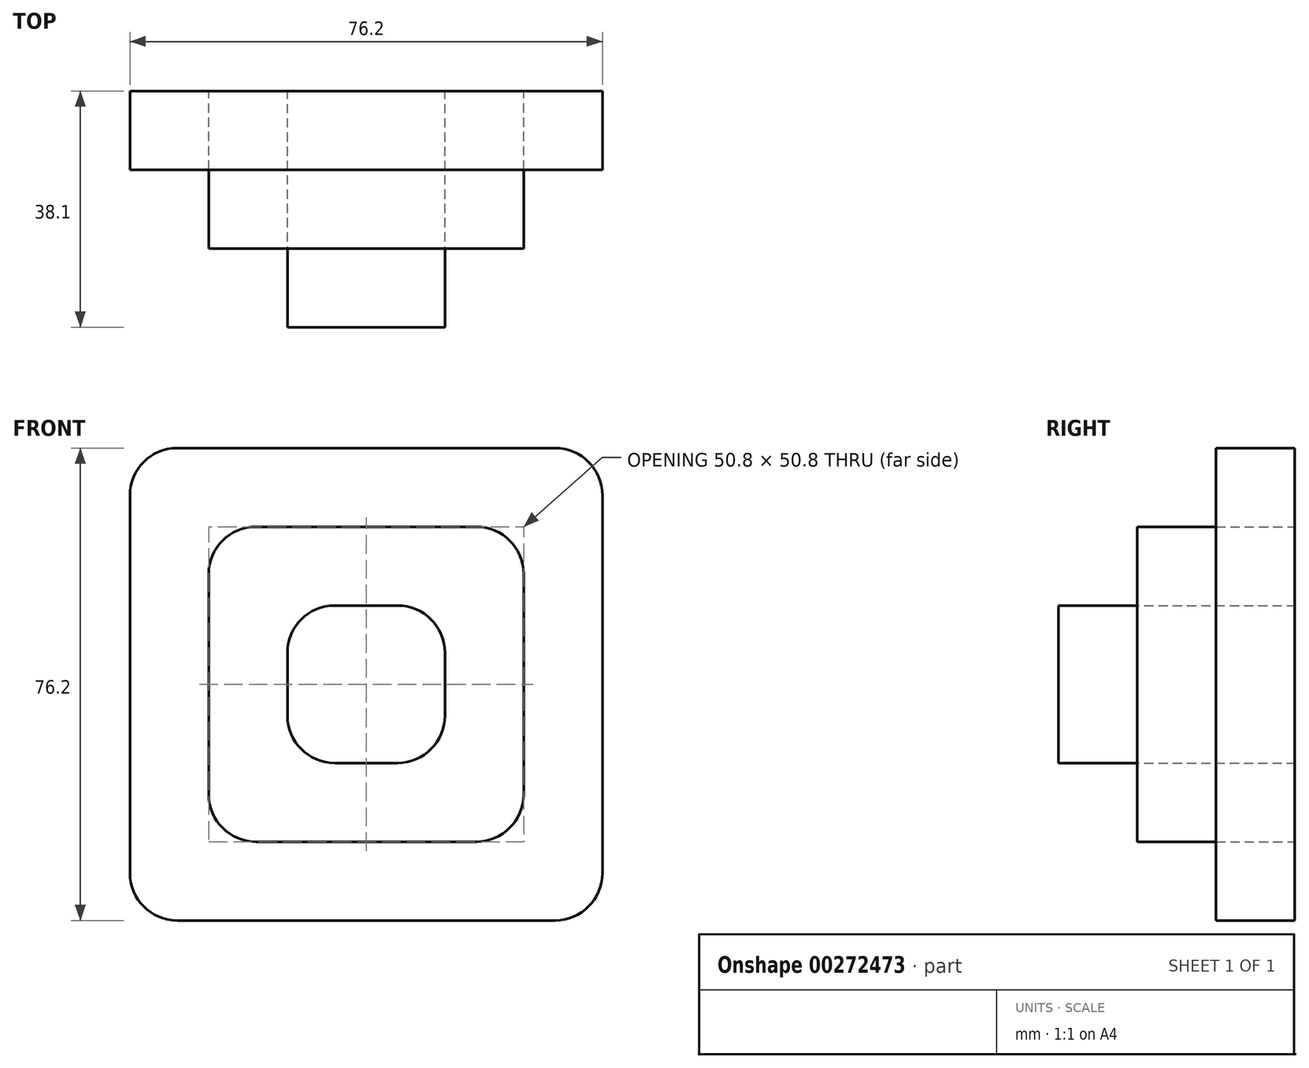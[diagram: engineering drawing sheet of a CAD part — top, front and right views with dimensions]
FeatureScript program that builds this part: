
annotation { "Feature Type Name" : "Feature", "Feature Type Description" : "" }
export const myFeature = defineFeature(function(context is Context, id is Id, definition is map)
    precondition{}
    {
        {
            var Q0;
            Q0=qCreatedBy(makeId("Front.planeOp"),FACE);
            var sketch = newSketch(context, id + "F0", { "sketchPlane" : qUnion([Q0])});
            skLineSegment(sketch, "E0.bottom", {"start": v(30.48, -38.1) * mm, "end": v(-30.48, -38.1) * mm});
            skLineSegment(sketch, "E0.top", {"start": v(30.48, 38.1) * mm, "end": v(-30.48, 38.1) * mm});
            skLineSegment(sketch, "E0.left", {"start": v(38.1, -30.48) * mm, "end": v(38.1, 30.48) * mm});
            skLineSegment(sketch, "E0.right", {"start": v(-38.1, -30.48) * mm, "end": v(-38.1, 30.48) * mm});
            skPoint(sketch, "E0.middle", {"position": v(0, 0) * mm});
            skPoint(sketch, "E1.visualSharp", {"position": v(-38.1, 38.1) * mm});
            skArc(sketch, "E1.filletArc", {"start": v(-30.48, 38.1) * mm, "mid": v(-35.87, 35.87) * mm, "end": v(-38.1, 30.48) * mm});
            skPoint(sketch, "E2.visualSharp", {"position": v(38.1, 38.1) * mm});
            skArc(sketch, "E2.filletArc", {"start": v(38.1, 30.48) * mm, "mid": v(35.87, 35.87) * mm, "end": v(30.48, 38.1) * mm});
            skPoint(sketch, "E3.visualSharp", {"position": v(38.1, -38.1) * mm});
            skArc(sketch, "E3.filletArc", {"start": v(30.48, -38.1) * mm, "mid": v(35.87, -35.87) * mm, "end": v(38.1, -30.48) * mm});
            skPoint(sketch, "E4.visualSharp", {"position": v(-38.1, -38.1) * mm});
            skArc(sketch, "E4.filletArc", {"start": v(-38.1, -30.48) * mm, "mid": v(-35.87, -35.87) * mm, "end": v(-30.48, -38.1) * mm});
            skLineSegment(sketch, "E5.bottom", {"start": v(17.78, -25.4) * mm, "end": v(-17.78, -25.4) * mm});
            skLineSegment(sketch, "E5.top", {"start": v(17.78, 25.4) * mm, "end": v(-17.78, 25.4) * mm});
            skLineSegment(sketch, "E5.left", {"start": v(25.4, -17.78) * mm, "end": v(25.4, 17.78) * mm});
            skLineSegment(sketch, "E5.right", {"start": v(-25.4, -17.78) * mm, "end": v(-25.4, 17.78) * mm});
            skPoint(sketch, "E6.visualSharp", {"position": v(-25.4, 25.4) * mm});
            skArc(sketch, "E6.filletArc", {"start": v(-17.78, 25.4) * mm, "mid": v(-23.17, 23.17) * mm, "end": v(-25.4, 17.78) * mm});
            skPoint(sketch, "E7.visualSharp", {"position": v(25.4, 25.4) * mm});
            skArc(sketch, "E7.filletArc", {"start": v(25.4, 17.78) * mm, "mid": v(23.17, 23.17) * mm, "end": v(17.78, 25.4) * mm});
            skPoint(sketch, "E8.visualSharp", {"position": v(25.4, -25.4) * mm});
            skArc(sketch, "E8.filletArc", {"start": v(17.78, -25.4) * mm, "mid": v(23.17, -23.17) * mm, "end": v(25.4, -17.78) * mm});
            skPoint(sketch, "E9.visualSharp", {"position": v(-25.4, -25.4) * mm});
            skArc(sketch, "E9.filletArc", {"start": v(-25.4, -17.78) * mm, "mid": v(-23.17, -23.17) * mm, "end": v(-17.78, -25.4) * mm});
            skLineSegment(sketch, "E10.bottom", {"start": v(5.08, -12.7) * mm, "end": v(-5.08, -12.7) * mm});
            skLineSegment(sketch, "E10.top", {"start": v(5.08, 12.7) * mm, "end": v(-5.08, 12.7) * mm});
            skLineSegment(sketch, "E10.left", {"start": v(12.7, -5.08) * mm, "end": v(12.7, 5.08) * mm});
            skLineSegment(sketch, "E10.right", {"start": v(-12.7, -5.08) * mm, "end": v(-12.7, 5.08) * mm});
            skPoint(sketch, "E11.visualSharp", {"position": v(-12.7, 12.7) * mm});
            skArc(sketch, "E11.filletArc", {"start": v(-5.08, 12.7) * mm, "mid": v(-10.47, 10.47) * mm, "end": v(-12.7, 5.08) * mm});
            skPoint(sketch, "E12.visualSharp", {"position": v(12.7, 12.7) * mm});
            skArc(sketch, "E12.filletArc", {"start": v(12.7, 5.08) * mm, "mid": v(10.47, 10.47) * mm, "end": v(5.08, 12.7) * mm});
            skPoint(sketch, "E13.visualSharp", {"position": v(12.7, -12.7) * mm});
            skArc(sketch, "E13.filletArc", {"start": v(5.08, -12.7) * mm, "mid": v(10.47, -10.47) * mm, "end": v(12.7, -5.08) * mm});
            skPoint(sketch, "E14.visualSharp", {"position": v(-12.7, -12.7) * mm});
            skArc(sketch, "E14.filletArc", {"start": v(-12.7, -5.08) * mm, "mid": v(-10.47, -10.47) * mm, "end": v(-5.08, -12.7) * mm});
            skSolve(sketch);
        }
        {
            var Q0;
            Q0=qSketchRegion(id+"F0",true);
            extrude(context, id + "F1", {"entities" : qUnion([Q0]), "depth" : 12.7 * mm});
        }
        {
            var Q0;
            Q0=makeQuery(id+"F0.imprint","IMPRINT",FACE,{"disambiguationData":[TD([[makeQuery(id+"F0.imprint","IMPRINT",EDGE,{"derivedFrom":sQuery(id+"F0.wireOp",EDGE,"E5.bottom")}),-1.0]])]});
            extrude(context, id + "F2", {"entities" : qUnion([Q0]), "depth" : 25.4 * mm});
        }
        {
            var Q0;
            Q0=makeQuery(id+"F0.imprint","IMPRINT",FACE,{"disambiguationData":[TD([[makeQuery(id+"F0.imprint","IMPRINT",EDGE,{"derivedFrom":sQuery(id+"F0.wireOp",EDGE,"E10.bottom")}),-1.0]])]});
            extrude(context, id + "F3", {"entities" : qUnion([Q0]), "depth" : 38.1 * mm});
        }
    });
